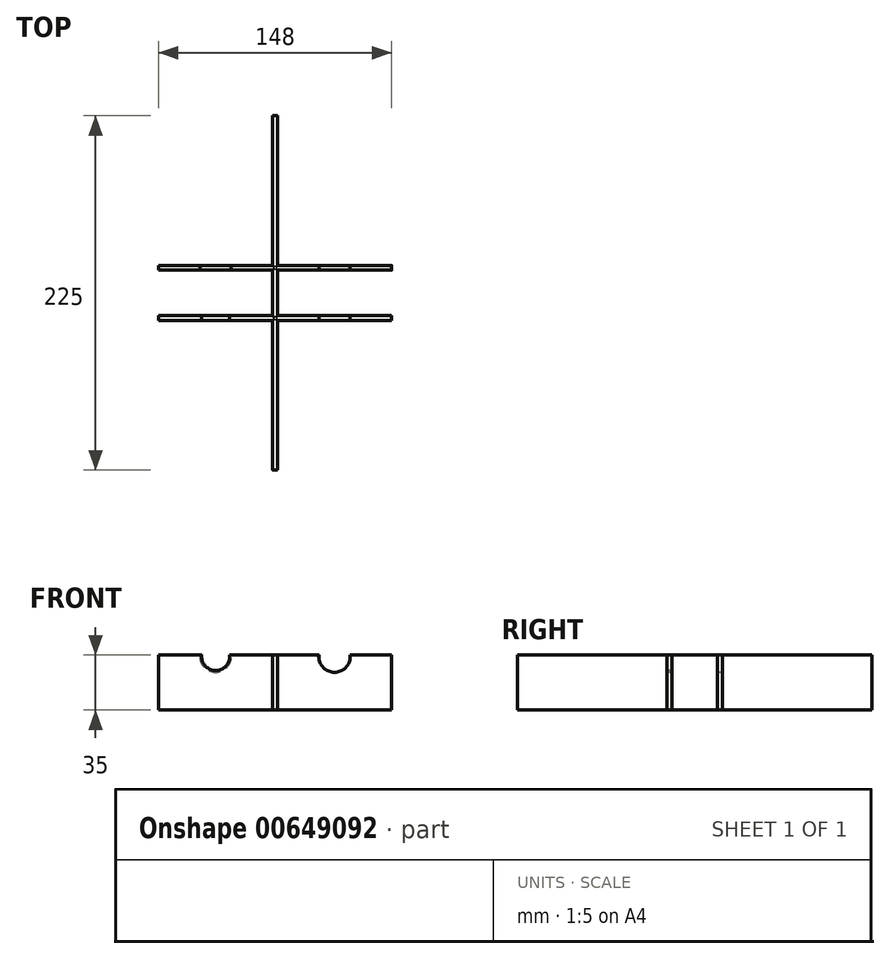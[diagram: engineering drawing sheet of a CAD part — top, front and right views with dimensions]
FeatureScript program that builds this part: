
annotation { "Feature Type Name" : "Feature", "Feature Type Description" : "" }
export const myFeature = defineFeature(function(context is Context, id is Id, definition is map)
    precondition{}
    {
        {
            var Q0;
            Q0=qCreatedBy(makeId("Top.planeOp"),FACE);
            var sketch = newSketch(context, id + "F0", { "sketchPlane" : qUnion([Q0])});
            skPoint(sketch, "E0.middle", {"position": v(0, 0) * mm});
            skLineSegment(sketch, "E1.bottom", {"start": v(1.5, 112.5) * mm, "end": v(-1.5, 112.5) * mm});
            skLineSegment(sketch, "E1.top", {"start": v(1.5, -112.5) * mm, "end": v(-1.5, -112.5) * mm});
            skLineSegment(sketch, "E2", {"start": v(-1.5, -17.5) * mm, "end": v(-74, -17.5) * mm});
            skLineSegment(sketch, "E3", {"start": v(-74, -17.5) * mm, "end": v(-74, -14.5) * mm});
            skLineSegment(sketch, "E4", {"start": v(-74, -14.5) * mm, "end": v(-1.5, -14.5) * mm});
            skLineSegment(sketch, "E5", {"start": v(1.5, -17.5) * mm, "end": v(74, -17.5) * mm});
            skLineSegment(sketch, "E6", {"start": v(74, -17.5) * mm, "end": v(74, -14.5) * mm});
            skLineSegment(sketch, "E7", {"start": v(74, -14.5) * mm, "end": v(1.5, -14.5) * mm});
            skLineSegment(sketch, "E8", {"start": v(-1.5, 14.5) * mm, "end": v(-74, 14.5) * mm});
            skLineSegment(sketch, "E9", {"start": v(-74, 14.5) * mm, "end": v(-74, 17.5) * mm});
            skLineSegment(sketch, "E10", {"start": v(-74, 17.5) * mm, "end": v(-1.5, 17.5) * mm});
            skLineSegment(sketch, "E11", {"start": v(74, 17.5) * mm, "end": v(74, 14.5) * mm});
            skLineSegment(sketch, "E12", {"start": v(74, 17.5) * mm, "end": v(1.5, 17.5) * mm});
            skLineSegment(sketch, "E13", {"start": v(74, 14.5) * mm, "end": v(1.5, 14.5) * mm});
            skLineSegment(sketch, "E14", {"start": v(-1.5, 112.5) * mm, "end": v(-1.5, 17.5) * mm});
            skLineSegment(sketch, "E15", {"start": v(-1.5, 14.5) * mm, "end": v(-1.5, -14.5) * mm});
            skLineSegment(sketch, "E16", {"start": v(-1.5, -17.5) * mm, "end": v(-1.5, -112.5) * mm});
            skLineSegment(sketch, "E17", {"start": v(1.5, 112.5) * mm, "end": v(1.5, 17.5) * mm});
            skLineSegment(sketch, "E18", {"start": v(1.5, 14.5) * mm, "end": v(1.5, -14.5) * mm});
            skLineSegment(sketch, "E19", {"start": v(1.5, -17.5) * mm, "end": v(1.5, -112.5) * mm});
            skSolve(sketch);
        }
        {
            var Q0;
            Q0=makeQuery(id+"F0.imprint","IMPRINT",FACE,{"disambiguationData":[TD([[makeQuery(id+"F0.imprint","IMPRINT",EDGE,{"derivedFrom":sQuery(id+"F0.wireOp",EDGE,"E1.bottom")}),1.0]])]});
            extrude(context, id + "F1", {"entities" : qUnion([Q0]), "depth" : 35 * mm, "offsetDistance" : 25 * mm});
        }
        {
            var Q0;
            Q0=makeQuery(id+"F1.opExtrude","CAP_EDGE",EDGE,{"disambiguationData":[OSD([sQuery(id+"F0.wireOp",EDGE,"E8")])],"isStart":false});
            var Q1;
            Q1=makeQuery(id+"F1.opExtrude","CAP_EDGE",EDGE,{"disambiguationData":[OSD([sQuery(id+"F0.wireOp",EDGE,"E14")])],"isStart":false});
            var Q2;
            Q2=makeQuery(id+"F1.opExtrude","CAP_EDGE",EDGE,{"disambiguationData":[OSD([sQuery(id+"F0.wireOp",EDGE,"E10")])],"isStart":false});
            var Q3;
            Q3=makeQuery(id+"F1.opExtrude","CAP_EDGE",EDGE,{"disambiguationData":[OSD([sQuery(id+"F0.wireOp",EDGE,"E17")])],"isStart":false});
            var Q4;
            Q4=makeQuery(id+"F1.opExtrude","CAP_EDGE",EDGE,{"disambiguationData":[OSD([sQuery(id+"F0.wireOp",EDGE,"E12")])],"isStart":false});
            var Q5;
            Q5=makeQuery(id+"F1.opExtrude","CAP_EDGE",EDGE,{"disambiguationData":[OSD([sQuery(id+"F0.wireOp",EDGE,"E13")])],"isStart":false});
            var Q6;
            Q6=makeQuery(id+"F1.opExtrude","CAP_EDGE",EDGE,{"disambiguationData":[OSD([sQuery(id+"F0.wireOp",EDGE,"E18")])],"isStart":false});
            var Q7;
            Q7=makeQuery(id+"F1.opExtrude","CAP_EDGE",EDGE,{"disambiguationData":[OSD([sQuery(id+"F0.wireOp",EDGE,"E15")])],"isStart":false});
            var Q8;
            Q8=makeQuery(id+"F1.opExtrude","CAP_EDGE",EDGE,{"disambiguationData":[OSD([sQuery(id+"F0.wireOp",EDGE,"E4")])],"isStart":false});
            var Q9;
            Q9=makeQuery(id+"F1.opExtrude","CAP_EDGE",EDGE,{"disambiguationData":[OSD([sQuery(id+"F0.wireOp",EDGE,"E2")])],"isStart":false});
            var Q10;
            Q10=makeQuery(id+"F1.opExtrude","CAP_EDGE",EDGE,{"disambiguationData":[OSD([sQuery(id+"F0.wireOp",EDGE,"E7")])],"isStart":false});
            var Q11;
            Q11=makeQuery(id+"F1.opExtrude","CAP_EDGE",EDGE,{"disambiguationData":[OSD([sQuery(id+"F0.wireOp",EDGE,"E5")])],"isStart":false});
            var Q12;
            Q12=makeQuery(id+"F1.opExtrude","CAP_EDGE",EDGE,{"disambiguationData":[OSD([sQuery(id+"F0.wireOp",EDGE,"E16")])],"isStart":false});
            var Q13;
            Q13=makeQuery(id+"F1.opExtrude","CAP_EDGE",EDGE,{"disambiguationData":[OSD([sQuery(id+"F0.wireOp",EDGE,"E19")])],"isStart":false});
            fillet(context, id + "F2", {"entities" : qUnion([Q0, Q1, Q2, Q3, Q4, Q5, Q6, Q7, Q8, Q9, Q10, Q11, Q12, Q13]), "radius" : 1 * mm, "tangentPropagation" : true, "allowEdgeOverflow" : false});
        }
        {
            var Q0;
            Q0=makeQuery(id+"F1.opExtrude","SWEPT_FACE",FACE,{"disambiguationData":[OSD([sQuery(id+"F0.wireOp",EDGE,"E2")])]});
            var sketch = newSketch(context, id + "F3", { "sketchPlane" : qUnion([Q0])});
            skCircle(sketch, "E20", {"center": v(-37.75, 34) * mm, "radius": 8.88 * mm});
            skSolve(sketch);
        }
        {
            var Q0;
            {var subQ0=sQuery(id+"F3.wireOp",EDGE,"E20");var subQ1=sQuery(id+"F0.wireOp",EDGE,"E2");var subQ2=makeQuery(id+"F2.opFillet","BLEND_EDGE",EDGE,{"blendedFrom":[makeQuery(id+"F1.opExtrude","CAP_EDGE",EDGE,{"disambiguationData":[OSD([subQ1])],"isStart":false}),makeQuery(id+"F1.opExtrude","SWEPT_FACE",FACE,{"disambiguationData":[OSD([subQ1])]})],"blendedInto":[makeQuery(id+"F1.opExtrude","SWEPT_FACE",FACE,{"disambiguationData":[OSD([subQ1])]})]});var subQ3=makeQuery(id+"F3.imprint","INTERSECT",VERTEX,{"disambiguationData":[OD(0.0)],"derivedFrom":[subQ2,subQ0]});Q0=makeQuery(id+"F3.imprint","IMPRINT",FACE,{"disambiguationData":[TD([[makeQuery(id+"F3.imprint","IMPRINT",EDGE,{"disambiguationData":[TD([[subQ3,1.0]])],"derivedFrom":subQ0}),1.0]])]});}
            var Q1;
            {var subQ0=sQuery(id+"F3.wireOp",EDGE,"E20");var subQ1=sQuery(id+"F0.wireOp",EDGE,"E2");var subQ2=makeQuery(id+"F2.opFillet","BLEND_EDGE",EDGE,{"blendedFrom":[makeQuery(id+"F1.opExtrude","CAP_EDGE",EDGE,{"disambiguationData":[OSD([subQ1])],"isStart":false}),makeQuery(id+"F1.opExtrude","SWEPT_FACE",FACE,{"disambiguationData":[OSD([subQ1])]})],"blendedInto":[makeQuery(id+"F1.opExtrude","SWEPT_FACE",FACE,{"disambiguationData":[OSD([subQ1])]})]});var subQ3=makeQuery(id+"F3.imprint","INTERSECT",VERTEX,{"disambiguationData":[OD(0.0)],"derivedFrom":[subQ2,subQ0]});Q1=makeQuery(id+"F3.imprint","IMPRINT",FACE,{"disambiguationData":[TD([[makeQuery(id+"F3.imprint","IMPRINT",EDGE,{"disambiguationData":[TD([[subQ3,-1.0]])],"derivedFrom":subQ0}),1.0]])]});}
            extrude(context, id + "F4", {"entities" : qUnion([Q0, Q1]), "operationType" : NewBodyOperationType.REMOVE, "oppositeDirection" : true, "depth" : 25 * mm, "offsetDistance" : 25 * mm});
        }
        {
            var Q0;
            Q0=makeQuery(id+"F1.opExtrude","SWEPT_FACE",FACE,{"disambiguationData":[OSD([sQuery(id+"F0.wireOp",EDGE,"E8")])]});
            var sketch = newSketch(context, id + "F5", { "sketchPlane" : qUnion([Q0])});
            skCircle(sketch, "E21", {"center": v(-37.75, 34) * mm, "radius": 10 * mm});
            skSolve(sketch);
        }
        {
            var Q0;
            {var subQ0=sQuery(id+"F5.wireOp",EDGE,"E21");var subQ1=sQuery(id+"F0.wireOp",EDGE,"E8");var subQ2=makeQuery(id+"F2.opFillet","BLEND_EDGE",EDGE,{"blendedFrom":[makeQuery(id+"F1.opExtrude","CAP_EDGE",EDGE,{"disambiguationData":[OSD([subQ1])],"isStart":false}),makeQuery(id+"F1.opExtrude","SWEPT_FACE",FACE,{"disambiguationData":[OSD([subQ1])]})],"blendedInto":[makeQuery(id+"F1.opExtrude","SWEPT_FACE",FACE,{"disambiguationData":[OSD([subQ1])]})]});var subQ3=makeQuery(id+"F5.imprint","INTERSECT",VERTEX,{"disambiguationData":[OD(0.0)],"derivedFrom":[subQ2,subQ0]});Q0=makeQuery(id+"F5.imprint","IMPRINT",FACE,{"disambiguationData":[TD([[makeQuery(id+"F5.imprint","IMPRINT",EDGE,{"disambiguationData":[TD([[subQ3,1.0]])],"derivedFrom":subQ0}),1.0]])]});}
            var Q1;
            {var subQ0=sQuery(id+"F5.wireOp",EDGE,"E21");var subQ1=sQuery(id+"F0.wireOp",EDGE,"E8");var subQ2=makeQuery(id+"F2.opFillet","BLEND_EDGE",EDGE,{"blendedFrom":[makeQuery(id+"F1.opExtrude","CAP_EDGE",EDGE,{"disambiguationData":[OSD([subQ1])],"isStart":false}),makeQuery(id+"F1.opExtrude","SWEPT_FACE",FACE,{"disambiguationData":[OSD([subQ1])]})],"blendedInto":[makeQuery(id+"F1.opExtrude","SWEPT_FACE",FACE,{"disambiguationData":[OSD([subQ1])]})]});var subQ3=makeQuery(id+"F5.imprint","INTERSECT",VERTEX,{"disambiguationData":[OD(0.0)],"derivedFrom":[subQ2,subQ0]});Q1=makeQuery(id+"F5.imprint","IMPRINT",FACE,{"disambiguationData":[TD([[makeQuery(id+"F5.imprint","IMPRINT",EDGE,{"disambiguationData":[TD([[subQ3,-1.0]])],"derivedFrom":subQ0}),1.0]])]});}
            extrude(context, id + "F6", {"entities" : qUnion([Q0, Q1]), "operationType" : NewBodyOperationType.REMOVE, "oppositeDirection" : true, "depth" : 25 * mm, "offsetDistance" : 25 * mm});
        }
        {
            var Q0;
            Q0=makeQuery(id+"F1.opExtrude","SWEPT_FACE",FACE,{"disambiguationData":[OSD([sQuery(id+"F0.wireOp",EDGE,"E5")])]});
            var sketch = newSketch(context, id + "F7", { "sketchPlane" : qUnion([Q0])});
            skCircle(sketch, "E22", {"center": v(37.75, 34) * mm, "radius": 10 * mm});
            skSolve(sketch);
        }
        {
            var Q0;
            {var subQ0=sQuery(id+"F7.wireOp",EDGE,"E22");var subQ1=sQuery(id+"F0.wireOp",EDGE,"E5");var subQ2=makeQuery(id+"F2.opFillet","BLEND_EDGE",EDGE,{"blendedFrom":[makeQuery(id+"F1.opExtrude","CAP_EDGE",EDGE,{"disambiguationData":[OSD([subQ1])],"isStart":false}),makeQuery(id+"F1.opExtrude","SWEPT_FACE",FACE,{"disambiguationData":[OSD([subQ1])]})],"blendedInto":[makeQuery(id+"F1.opExtrude","SWEPT_FACE",FACE,{"disambiguationData":[OSD([subQ1])]})]});var subQ3=makeQuery(id+"F7.imprint","INTERSECT",VERTEX,{"disambiguationData":[OD(0.0)],"derivedFrom":[subQ2,subQ0]});Q0=makeQuery(id+"F7.imprint","IMPRINT",FACE,{"disambiguationData":[TD([[makeQuery(id+"F7.imprint","IMPRINT",EDGE,{"disambiguationData":[TD([[subQ3,-1.0]])],"derivedFrom":subQ0}),1.0]])]});}
            var Q1;
            {var subQ0=sQuery(id+"F7.wireOp",EDGE,"E22");var subQ1=sQuery(id+"F0.wireOp",EDGE,"E5");var subQ2=makeQuery(id+"F2.opFillet","BLEND_EDGE",EDGE,{"blendedFrom":[makeQuery(id+"F1.opExtrude","CAP_EDGE",EDGE,{"disambiguationData":[OSD([subQ1])],"isStart":false}),makeQuery(id+"F1.opExtrude","SWEPT_FACE",FACE,{"disambiguationData":[OSD([subQ1])]})],"blendedInto":[makeQuery(id+"F1.opExtrude","SWEPT_FACE",FACE,{"disambiguationData":[OSD([subQ1])]})]});var subQ3=makeQuery(id+"F7.imprint","INTERSECT",VERTEX,{"disambiguationData":[OD(0.0)],"derivedFrom":[subQ2,subQ0]});Q1=makeQuery(id+"F7.imprint","IMPRINT",FACE,{"disambiguationData":[TD([[makeQuery(id+"F7.imprint","IMPRINT",EDGE,{"disambiguationData":[TD([[subQ3,1.0]])],"derivedFrom":subQ0}),1.0]])]});}
            extrude(context, id + "F8", {"entities" : qUnion([Q0, Q1]), "operationType" : NewBodyOperationType.REMOVE, "endBound" : BoundingType.THROUGH_ALL, "oppositeDirection" : true, "depth" : 25 * mm, "offsetDistance" : 25 * mm});
        }
    });
